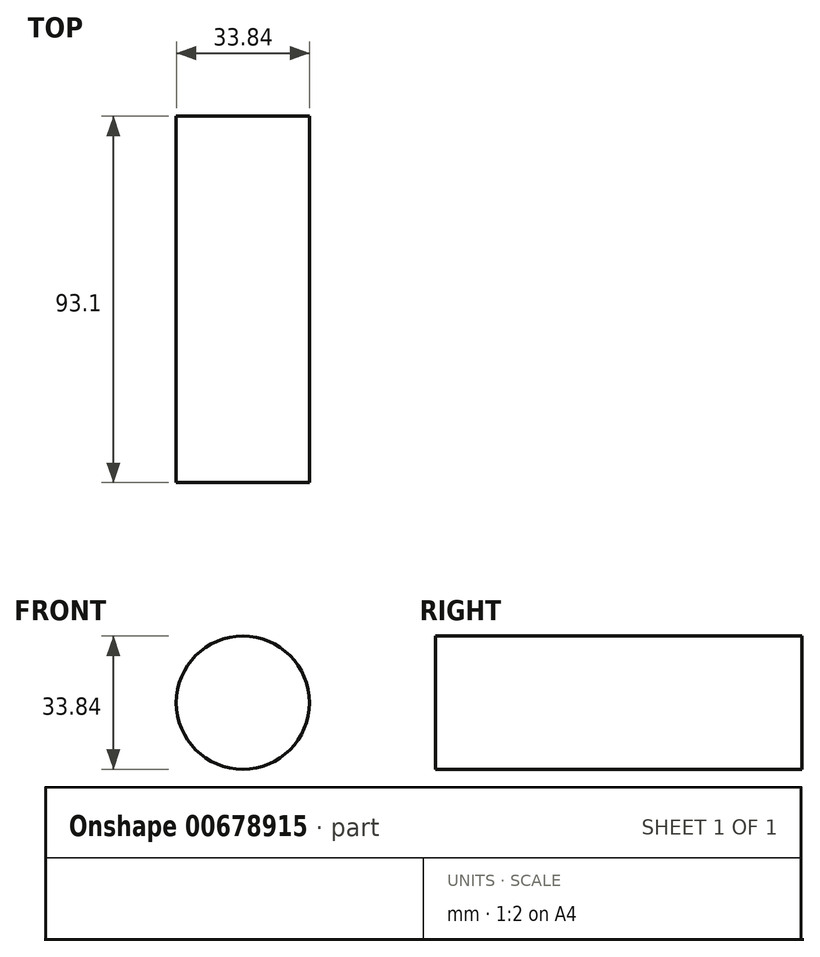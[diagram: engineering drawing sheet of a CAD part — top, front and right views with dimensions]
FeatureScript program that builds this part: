
annotation { "Feature Type Name" : "Feature", "Feature Type Description" : "" }
export const myFeature = defineFeature(function(context is Context, id is Id, definition is map)
    precondition{}
    {
        {
            var Q0;
            Q0=qCreatedBy(makeId("Front.planeOp"),FACE);
            var sketch = newSketch(context, id + "F0", { "sketchPlane" : qUnion([Q0])});
            skCircle(sketch, "E0", {"center": v(0, 0) * mm, "radius": 16.92 * mm});
            skSolve(sketch);
        }
        {
            var Q0;
            Q0 = qSketchRegion(id + "F0", true);
            extrude(context, id + "F1", {"entities" : qUnion([Q0]), "depth" : 93.1 * mm, "offsetDistance" : 25 * mm});
        }
    });
